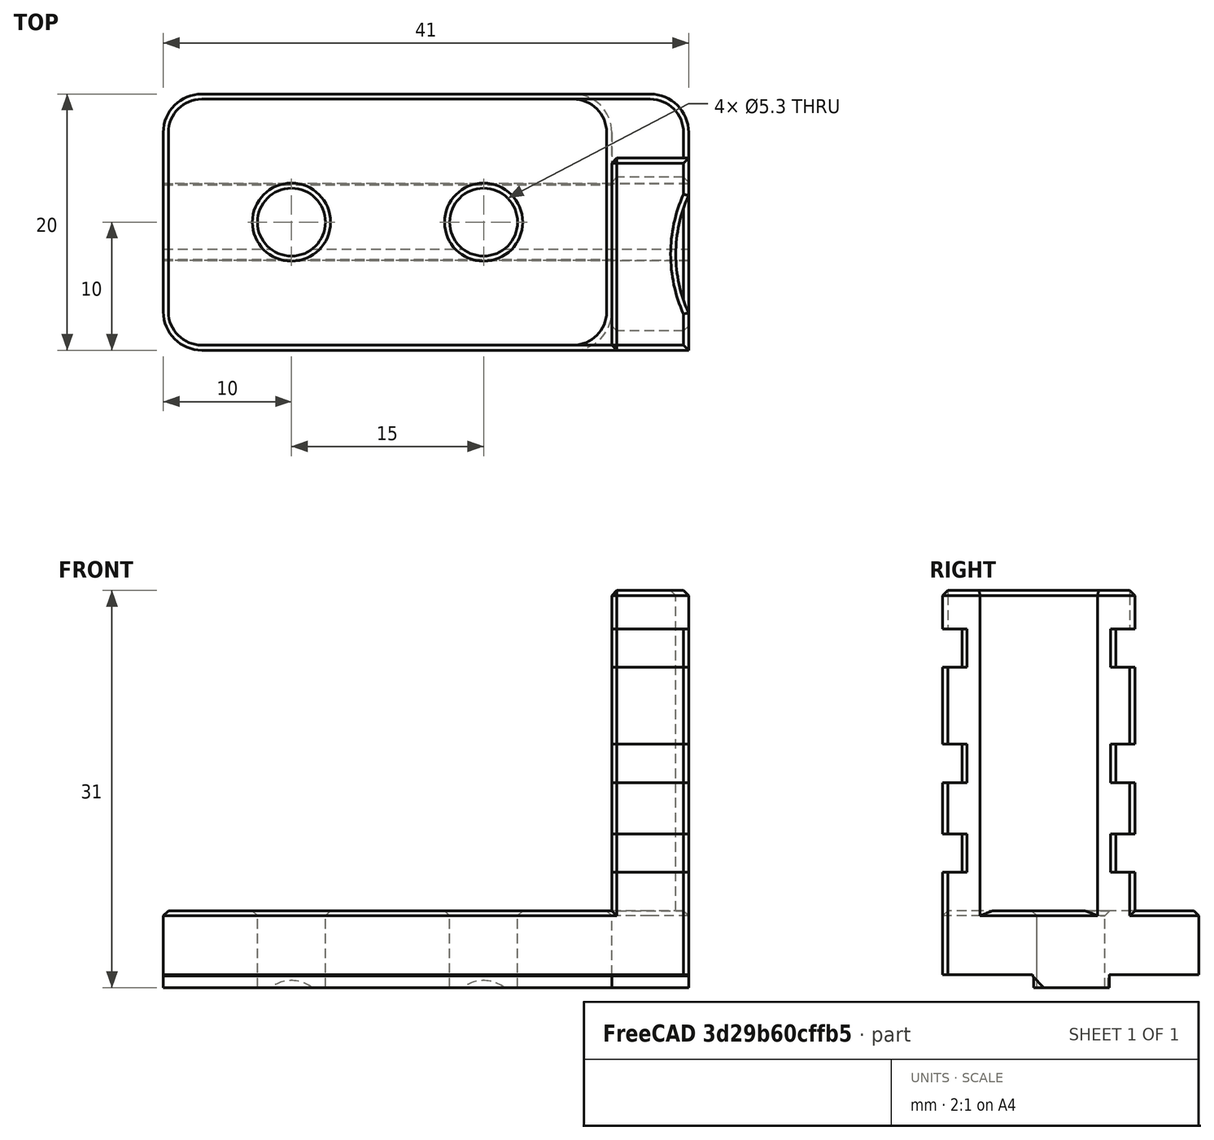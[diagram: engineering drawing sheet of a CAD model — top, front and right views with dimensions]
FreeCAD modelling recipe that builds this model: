
FCSTD DOCUMENT  (FreeCAD 0.19R24291 (Git))
Label: back-gantry-stopper
License: Other
LicenseURL: GPL3
objects: Part::Box×5, Part::MultiFuse×5, Part::Cylinder×4, Part::Chamfer×4, Part::Cut×3, Part::Fillet×2, Part::Feature×1
note: 24 computed .brp shape members not serialized (recipe doc carries the construction recipe); baked Part::Feature solids carry a one-line shape summary decoded from their .brp

FEATURE [Part::Box] Box  label="Cube"
  AttacherType = Attacher::AttachEngine3D
  Height = 5
  Length = 35
  Placement = pos=(-5,0,0) rot=(0,0,1;0rad)
  Width = 20
FEATURE [Part::Cylinder] Cylinder
  Angle = 360
  AttacherType = Attacher::AttachEngine3D
  Height = 14
  Placement = pos=(5,10,-5) rot=(0,0,1;0rad)
  Radius = 2.65
FEATURE [Part::Cylinder] Cylinder001
  Angle = 360
  AttacherType = Attacher::AttachEngine3D
  Height = 14
  Placement = pos=(20,10,-5) rot=(0,0,1;0rad)
  Radius = 2.65
FEATURE [Part::Box] Box001  label="Cube001"
  AttacherType = Attacher::AttachEngine3D
  Height = 2
  Length = 35
  Placement = pos=(-5,7.1,-1) rot=(0,0,1;0rad)
  Width = 5.8
FEATURE [Part::MultiFuse] Fusion001
  Shapes = -> [Cylinder,Cylinder001]
FEATURE [Part::Fillet] Fillet
  Base = -> Box
  Edges = 4 edges r=3: [Edge1,Edge3,Edge5,Edge7]
FEATURE [Part::MultiFuse] Fusion
  Shapes = -> [Box001,Fillet]
FEATURE [Part::Cut] Cut
  Base = -> Fusion
  Tool = -> Fusion001
FEATURE [Part::Chamfer] Chamfer
  Base = -> Cut
  Edges = 10 edges r=0.4: [Edge23,Edge31,Edge33,Edge38,Edge42,Edge44,Edge45,Edge46,Edge47,Edge48]
FEATURE [Part::Feature] Chamfer005
  Placement = pos=(33,15,-2) rot=(0,-0.707107,0.707107;3.14159rad)
  shape: bbox 6 x 15 x 35 mm, 68 faces (baked)
FEATURE [Part::Cylinder] Cylinder002
  Angle = 360
  AttacherType = Attacher::AttachEngine3D
  Height = 14
  Placement = pos=(5,10,-5) rot=(0,0,1;0rad)
  Radius = 2.65
FEATURE [Part::Box] Box002  label="Cube002"
  AttacherType = Attacher::AttachEngine3D
  Height = 2
  Length = 41
  Placement = pos=(-5,7,-1) rot=(0,0,1;0rad)
  Width = 6
FEATURE [Part::Cylinder] Cylinder003
  Angle = 360
  AttacherType = Attacher::AttachEngine3D
  Height = 14
  Placement = pos=(20,10,-5) rot=(0,0,1;0rad)
  Radius = 2.65
FEATURE [Part::MultiFuse] Fusion002
  Shapes = -> [Cylinder002,Cylinder003]
FEATURE [Part::Box] Box003  label="Cube003"
  AttacherType = Attacher::AttachEngine3D
  Height = 5
  Length = 41
  Placement = pos=(-5,0,0) rot=(0,0,1;0rad)
  Width = 20
FEATURE [Part::Chamfer] Chamfer006
  Base = -> Box003
  Edges = 1 edges r=0.4: [Edge5]
FEATURE [Part::Fillet] Fillet001
  Base = -> Chamfer006
  Edges = 3 edges r=3: [Edge4,Edge12,Edge15]
FEATURE [Part::Box] Box004  label="Cube004"
  AttacherType = Attacher::AttachEngine3D
  Height = 10
  Length = 10
  Placement = pos=(28,0,-10) rot=(0,0,1;0rad)
  Width = 17
FEATURE [Part::Cut] Cut001
  Base = -> Chamfer005
  Tool = -> Box004
FEATURE [Part::Chamfer] Chamfer007
  Base = -> Box002
  Edges = 1 edges r=0.9: [Edge9]
FEATURE [Part::MultiFuse] Fusion003
  Shapes = -> [Fillet001,Chamfer007]
FEATURE [Part::Cut] Cut002
  Base = -> Fusion003
  Tool = -> Fusion002
FEATURE [Part::Chamfer] Chamfer008
  Base = -> Cut002
  Edges = 10 edges r=0.4: [Edge8,Edge11,Edge22,Edge24,Edge25,Edge26,Edge27,Edge28,Edge29,Edge30]
FEATURE [Part::MultiFuse] Fusion004
  Shapes = -> [Chamfer008,Cut001]
